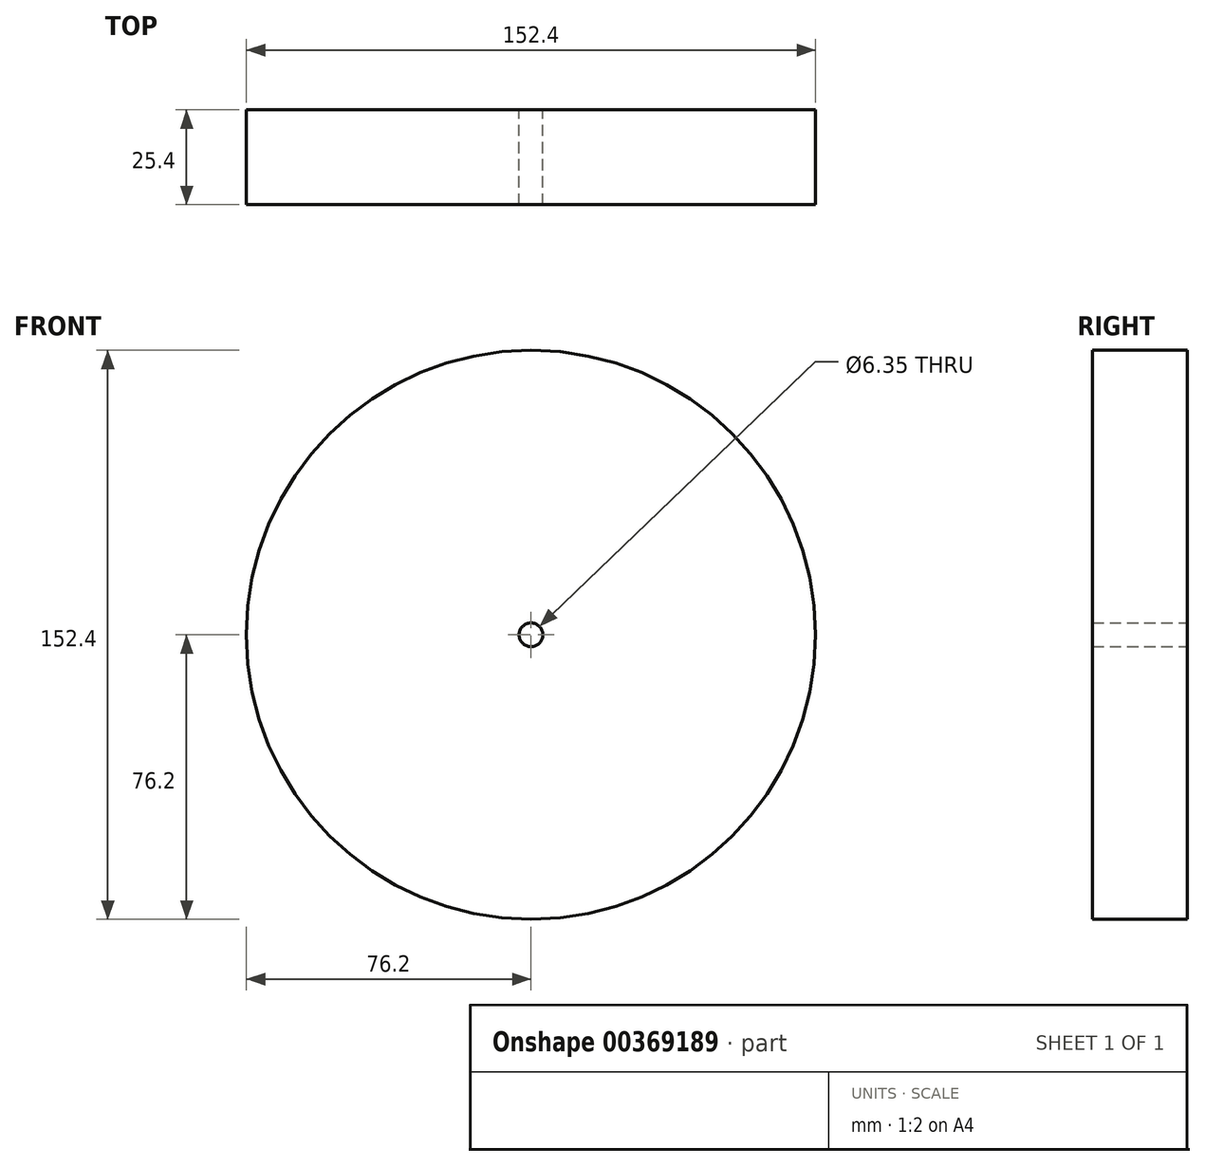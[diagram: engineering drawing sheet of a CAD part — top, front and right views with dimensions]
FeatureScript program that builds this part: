
annotation { "Feature Type Name" : "Feature", "Feature Type Description" : "" }
export const myFeature = defineFeature(function(context is Context, id is Id, definition is map)
    precondition{}
    {
        {
            var Q0;
            Q0=qCreatedBy(makeId("Front.planeOp"),FACE);
            var sketch = newSketch(context, id + "F0", { "sketchPlane" : qUnion([Q0])});
            skCircle(sketch, "E0", {"center": v(0, 0) * mm, "radius": 76.2 * mm});
            skCircle(sketch, "E1", {"center": v(0, 0) * mm, "radius": 3.18 * mm});
            skSolve(sketch);
        }
        {
            var Q0;
            Q0 = qSketchRegion(id + "F0", true);
            extrude(context, id + "F1", {"entities" : qUnion([Q0]), "depth" : 25.4 * mm, "symmetric" : true});
        }
    });
